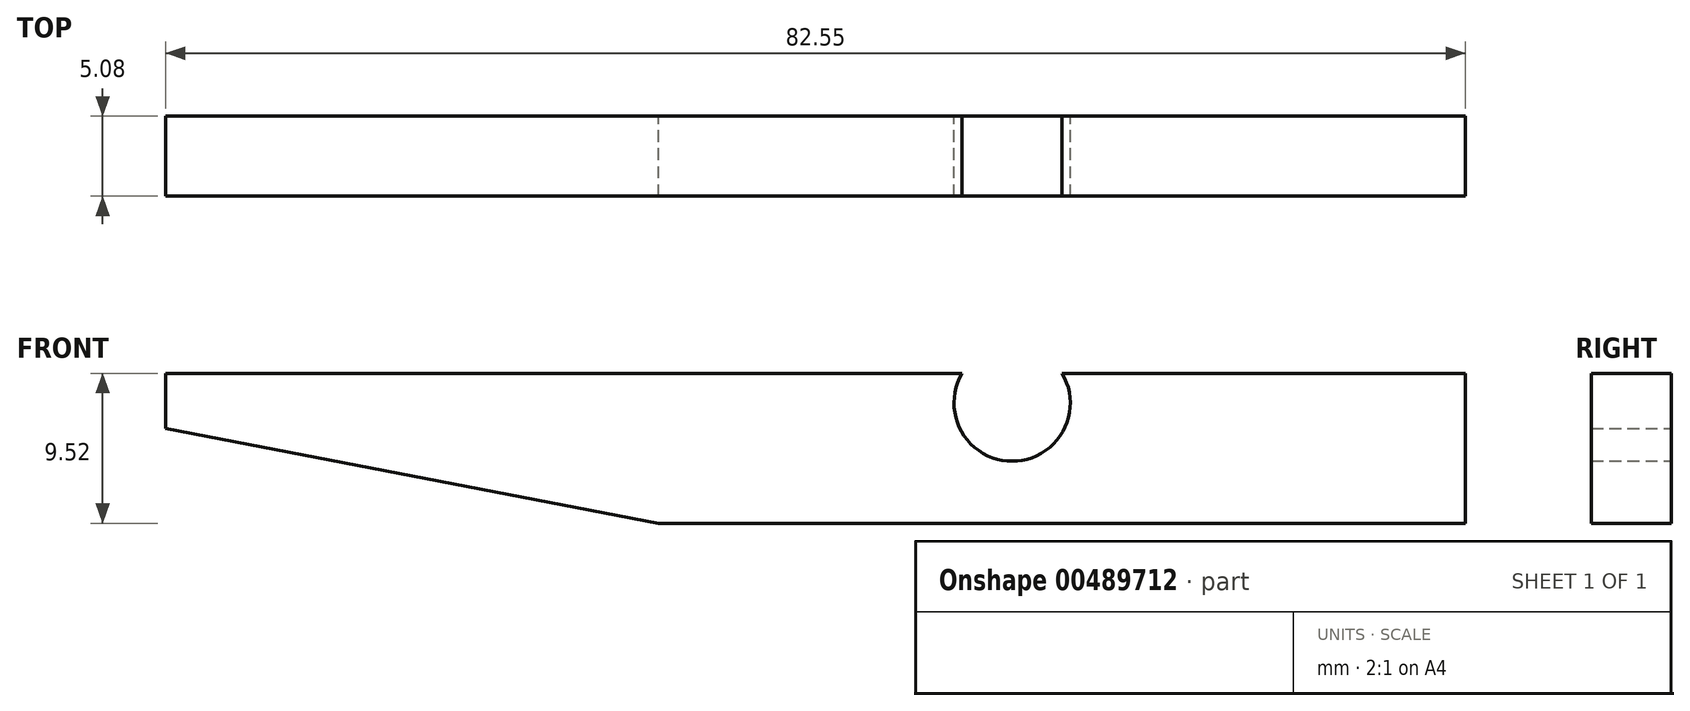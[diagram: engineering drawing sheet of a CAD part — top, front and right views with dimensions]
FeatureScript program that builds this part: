
annotation { "Feature Type Name" : "Feature", "Feature Type Description" : "" }
export const myFeature = defineFeature(function(context is Context, id is Id, definition is map)
    precondition{}
    {
        {
            var Q0;
            Q0=qCreatedBy(makeId("Front.planeOp"),FACE);
            var sketch = newSketch(context, id + "F0", { "sketchPlane" : qUnion([Q0])});
            skLineSegment(sketch, "E0.bottom", {"start": v(9.1, -15.46) * mm, "end": v(-42.16, -15.46) * mm});
            skLineSegment(sketch, "E0.top", {"start": v(9.1, -5.94) * mm, "end": v(-16.52, -5.94) * mm});
            skLineSegment(sketch, "E0.left", {"start": v(9.1, -15.46) * mm, "end": v(9.1, -5.94) * mm});
            skLineSegment(sketch, "E0.right", {"start": v(-73.46, -9.43) * mm, "end": v(-73.46, -5.94) * mm});
            skPoint(sketch, "E0.middle", {"position": v(-32.18, -10.7) * mm});
            skLineSegment(sketch, "E1.trimOffspring", {"start": v(-22.87, -5.94) * mm, "end": v(-73.46, -5.94) * mm});
            skLineSegment(sketch, "E2", {"start": v(-73.46, -9.43) * mm, "end": v(-42.16, -15.46) * mm});
            skPoint(sketch, "E3.orphan", {"position": v(-73.46, -15.46) * mm});
            skArc(sketch, "E4", {"start": v(-22.87, -5.94) * mm, "mid": v(-19.7, -11.52) * mm, "end": v(-16.52, -5.94) * mm});
            skPoint(sketch, "E5.center.orphan", {"position": v(-19.7, -5.94) * mm});
            skSolve(sketch);
        }
        {
            var Q0;
            Q0=makeQuery(id+"F0.imprint","IMPRINT",FACE,{"disambiguationData":[TD([[makeQuery(id+"F0.imprint","IMPRINT",EDGE,{"derivedFrom":sQuery(id+"F0.wireOp",EDGE,"E0.bottom")}),-1.0]])]});
            extrude(context, id + "F1", {"entities" : qUnion([Q0]), "depth" : 5.08 * mm});
        }
    });
